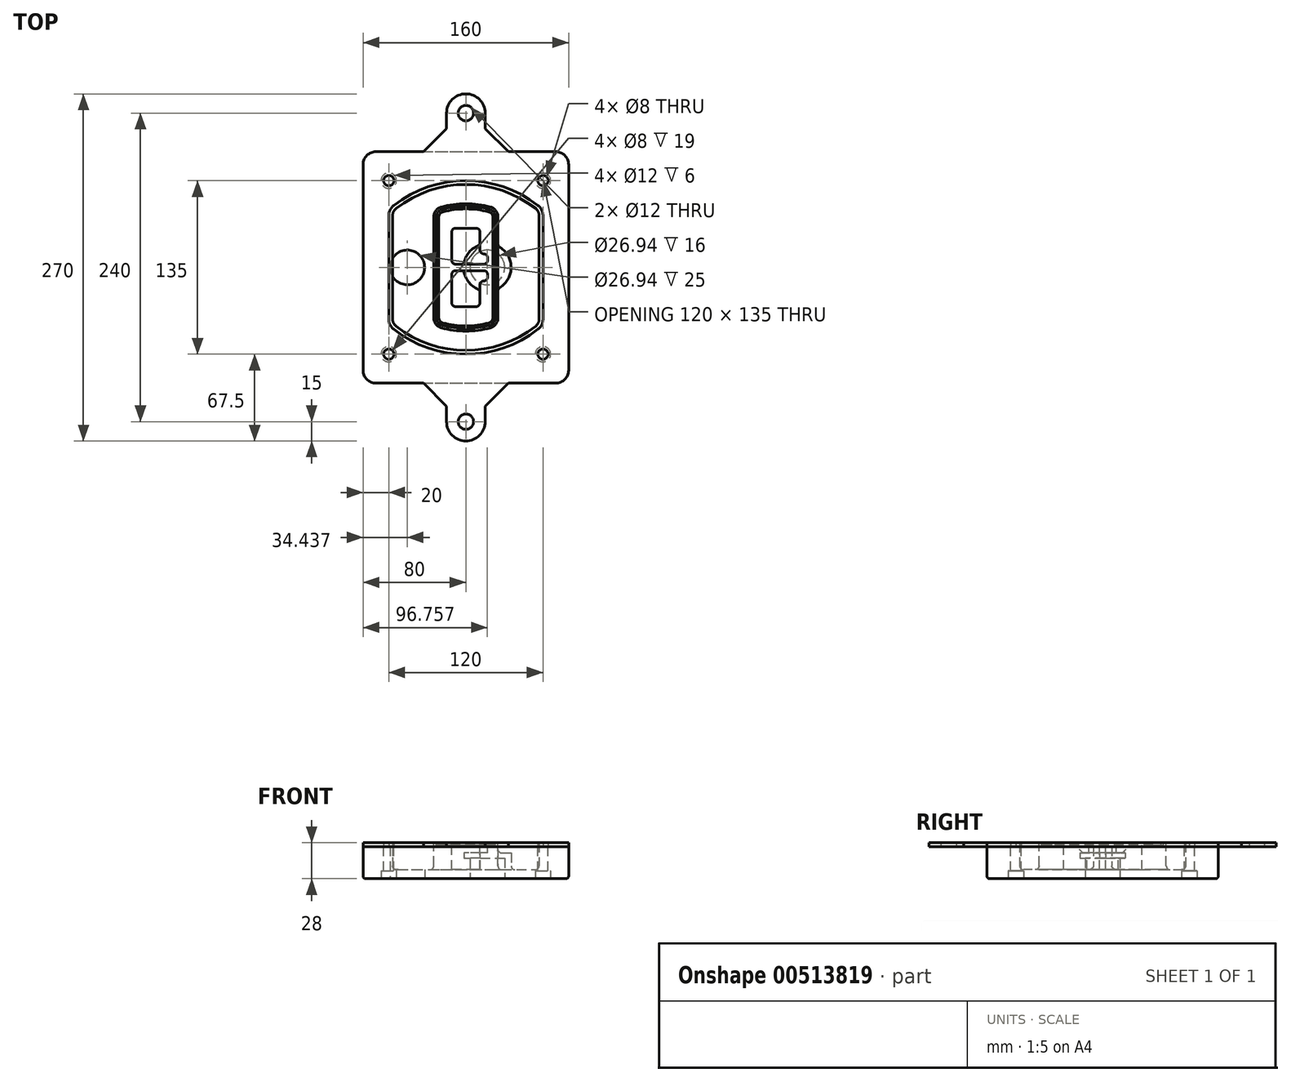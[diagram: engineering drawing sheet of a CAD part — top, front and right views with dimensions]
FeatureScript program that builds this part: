
annotation { "Feature Type Name" : "Feature", "Feature Type Description" : "" }
export const myFeature = defineFeature(function(context is Context, id is Id, definition is map)
    precondition{}
    {
        {
            var Q0;
            Q0=qCreatedBy(makeId("Top.planeOp"),FACE);
            var sketch = newSketch(context, id + "F0", { "sketchPlane" : qUnion([Q0])});
            skPoint(sketch, "E0.rect.middle", {"position": v(0, 0) * mm});
            skLineSegment(sketch, "E1.bottom", {"start": v(-70, -90) * mm, "end": v(70, -90) * mm});
            skLineSegment(sketch, "E1.top", {"start": v(-70, 90) * mm, "end": v(70, 90) * mm});
            skLineSegment(sketch, "E1.left", {"start": v(-80, -80) * mm, "end": v(-80, 80) * mm});
            skLineSegment(sketch, "E1.right", {"start": v(80, -80) * mm, "end": v(80, 80) * mm});
            skLineSegment(sketch, "E2", {"start": v(-80, 90) * mm, "end": v(80, -90) * mm, "construction": true});
            skLineSegment(sketch, "E3", {"start": v(80, 90) * mm, "end": v(-80, -90) * mm, "construction": true});
            skCircle(sketch, "E4", {"center": v(-60, 67.5) * mm, "radius": 4 * mm});
            skCircle(sketch, "E5", {"center": v(60, 67.5) * mm, "radius": 4 * mm});
            skCircle(sketch, "E6", {"center": v(60, -67.5) * mm, "radius": 4 * mm});
            skCircle(sketch, "E7", {"center": v(-60, -67.5) * mm, "radius": 4 * mm});
            skLineSegment(sketch, "E8", {"start": v(-60, 67.5) * mm, "end": v(60, 67.5) * mm, "construction": true});
            skLineSegment(sketch, "E9", {"start": v(60, 67.5) * mm, "end": v(60, -67.5) * mm, "construction": true});
            skLineSegment(sketch, "E10", {"start": v(60, -67.5) * mm, "end": v(-60, -67.5) * mm, "construction": true});
            skLineSegment(sketch, "E11", {"start": v(-60, -67.5) * mm, "end": v(-60, 67.5) * mm, "construction": true});
            skLineSegment(sketch, "E12", {"start": v(-60, 40.3) * mm, "end": v(-60, -40.3) * mm});
            skLineSegment(sketch, "E13", {"start": v(60, 40.3) * mm, "end": v(60, -40.3) * mm});
            skArc(sketch, "E14", {"start": v(56.15, 48.18) * mm, "mid": v(0, 67.5) * mm, "end": v(-56.15, 48.18) * mm});
            skArc(sketch, "E15", {"start": v(-56.15, -48.18) * mm, "mid": v(0, -67.5) * mm, "end": v(56.15, -48.18) * mm});
            skLineSegment(sketch, "E16", {"start": v(-60, 0) * mm, "end": v(60, 0) * mm, "construction": true});
            skPoint(sketch, "E17.visualSharp", {"position": v(-60, -45) * mm});
            skArc(sketch, "E17.filletArc", {"start": v(-60, -40.3) * mm, "mid": v(-58.99, -44.68) * mm, "end": v(-56.15, -48.18) * mm});
            skPoint(sketch, "E18.visualSharp", {"position": v(-60, 45) * mm});
            skArc(sketch, "E18.filletArc", {"start": v(-56.15, 48.18) * mm, "mid": v(-58.99, 44.68) * mm, "end": v(-60, 40.3) * mm});
            skPoint(sketch, "E19.visualSharp", {"position": v(60, 45) * mm});
            skArc(sketch, "E19.filletArc", {"start": v(60, 40.3) * mm, "mid": v(58.99, 44.68) * mm, "end": v(56.15, 48.18) * mm});
            skPoint(sketch, "E20.visualSharp", {"position": v(60, -45) * mm});
            skArc(sketch, "E20.filletArc", {"start": v(56.15, -48.18) * mm, "mid": v(58.99, -44.68) * mm, "end": v(60, -40.3) * mm});
            skPoint(sketch, "E21.visualSharp", {"position": v(-80, 90) * mm});
            skArc(sketch, "E21.filletArc", {"start": v(-70, 90) * mm, "mid": v(-77.07, 87.07) * mm, "end": v(-80, 80) * mm});
            skPoint(sketch, "E22.visualSharp", {"position": v(80, 90) * mm});
            skArc(sketch, "E22.filletArc", {"start": v(80, 80) * mm, "mid": v(77.07, 87.07) * mm, "end": v(70, 90) * mm});
            skPoint(sketch, "E23.visualSharp", {"position": v(80, -90) * mm});
            skArc(sketch, "E23.filletArc", {"start": v(70, -90) * mm, "mid": v(77.07, -87.07) * mm, "end": v(80, -80) * mm});
            skPoint(sketch, "E24.visualSharp", {"position": v(-80, -90) * mm});
            skArc(sketch, "E24.filletArc", {"start": v(-80, -80) * mm, "mid": v(-77.07, -87.07) * mm, "end": v(-70, -90) * mm});
            skArc(sketch, "E25.0", {"start": v(57, 40.3) * mm, "mid": v(56.3, 43.36) * mm, "end": v(54.3, 45.81) * mm});
            skLineSegment(sketch, "E25.1", {"start": v(57, 40.3) * mm, "end": v(57, -40.3) * mm});
            skArc(sketch, "E25.2", {"start": v(54.3, -45.81) * mm, "mid": v(56.3, -43.36) * mm, "end": v(57, -40.3) * mm});
            skArc(sketch, "E25.3", {"start": v(-54.3, -45.81) * mm, "mid": v(0, -64.5) * mm, "end": v(54.3, -45.81) * mm});
            skArc(sketch, "E25.4", {"start": v(-57, -40.3) * mm, "mid": v(-56.3, -43.36) * mm, "end": v(-54.3, -45.81) * mm});
            skArc(sketch, "E25.5", {"start": v(54.3, 45.81) * mm, "mid": v(0, 64.5) * mm, "end": v(-54.3, 45.81) * mm});
            skLineSegment(sketch, "E25.6", {"start": v(-57, 40.3) * mm, "end": v(-57, -40.3) * mm});
            skArc(sketch, "E25.7", {"start": v(-54.3, 45.81) * mm, "mid": v(-56.3, 43.36) * mm, "end": v(-57, 40.3) * mm});
            skArc(sketch, "E26.0", {"start": v(-58.62, 51.33) * mm, "mid": v(-62.58, 46.43) * mm, "end": v(-64, 40.3) * mm});
            skArc(sketch, "E26.1", {"start": v(58.62, 51.33) * mm, "mid": v(0, 71.5) * mm, "end": v(-58.62, 51.33) * mm});
            skArc(sketch, "E26.2", {"start": v(64, 40.3) * mm, "mid": v(62.58, 46.43) * mm, "end": v(58.62, 51.33) * mm});
            skLineSegment(sketch, "E26.3", {"start": v(64, 40.3) * mm, "end": v(64, -40.3) * mm});
            skArc(sketch, "E26.4", {"start": v(58.62, -51.33) * mm, "mid": v(62.58, -46.43) * mm, "end": v(64, -40.3) * mm});
            skLineSegment(sketch, "E26.5", {"start": v(-64, 40.3) * mm, "end": v(-64, -40.3) * mm});
            skArc(sketch, "E26.6", {"start": v(-58.62, -51.33) * mm, "mid": v(0, -71.5) * mm, "end": v(58.62, -51.33) * mm});
            skArc(sketch, "E26.7", {"start": v(-64, -40.3) * mm, "mid": v(-62.58, -46.43) * mm, "end": v(-58.62, -51.33) * mm});
            skSolve(sketch);
        }
        {
            var Q0;
            Q0=makeQuery(id+"F0.imprint","IMPRINT",FACE,{"disambiguationData":[TD([[makeQuery(id+"F0.imprint","IMPRINT",EDGE,{"derivedFrom":sQuery(id+"F0.wireOp",EDGE,"E1.bottom")}),1.0]])]});
            var Q1;
            Q1=makeQuery(id+"F0.imprint","IMPRINT",FACE,{"disambiguationData":[TD([[makeQuery(id+"F0.imprint","IMPRINT",EDGE,{"derivedFrom":sQuery(id+"F0.wireOp",EDGE,"E12")}),1.0]])]});
            var Q2;
            Q2=makeQuery(id+"F0.imprint","IMPRINT",FACE,{"disambiguationData":[TD([[makeQuery(id+"F0.imprint","IMPRINT",EDGE,{"derivedFrom":sQuery(id+"F0.wireOp",EDGE,"E25.0")}),1.0]])]});
            var Q3;
            Q3=makeQuery(id+"F0.imprint","IMPRINT",FACE,{"disambiguationData":[TD([[makeQuery(id+"F0.imprint","IMPRINT",EDGE,{"derivedFrom":sQuery(id+"F0.wireOp",EDGE,"E12")}),-1.0]])]});
            extrude(context, id + "F1", {"entities" : qUnion([Q0, Q1, Q2, Q3]), "oppositeDirection" : true, "depth" : 25 * mm});
        }
        {
            var Q0;
            Q0=makeQuery(id+"F0.imprint","IMPRINT",FACE,{"disambiguationData":[TD([[makeQuery(id+"F0.imprint","IMPRINT",EDGE,{"derivedFrom":sQuery(id+"F0.wireOp",EDGE,"E12")}),1.0]])]});
            extrude(context, id + "F2", {"entities" : qUnion([Q0]), "operationType" : NewBodyOperationType.ADD, "depth" : 3 * mm});
        }
        {
            var Q0;
            Q0=makeQuery(id+"F0.imprint","IMPRINT",FACE,{"disambiguationData":[TD([[makeQuery(id+"F0.imprint","IMPRINT",EDGE,{"derivedFrom":sQuery(id+"F0.wireOp",EDGE,"E25.0")}),1.0]])]});
            extrude(context, id + "F3", {"entities" : qUnion([Q0]), "operationType" : NewBodyOperationType.REMOVE, "oppositeDirection" : true, "depth" : 18 * mm});
        }
        {
            var Q0;
            Q0=makeQuery(id+"F2.opExtrude","CAP_FACE",FACE,{"disambiguationData":[OSD([sQuery(id+"F0.wireOp",EDGE,"E12"),sQuery(id+"F0.wireOp",EDGE,"E13"),sQuery(id+"F0.wireOp",EDGE,"E14"),sQuery(id+"F0.wireOp",EDGE,"E15"),sQuery(id+"F0.wireOp",EDGE,"E17.filletArc"),sQuery(id+"F0.wireOp",EDGE,"E18.filletArc"),sQuery(id+"F0.wireOp",EDGE,"E19.filletArc"),sQuery(id+"F0.wireOp",EDGE,"E20.filletArc"),sQuery(id+"F0.wireOp",EDGE,"E25.0"),sQuery(id+"F0.wireOp",EDGE,"E25.1"),sQuery(id+"F0.wireOp",EDGE,"E25.2"),sQuery(id+"F0.wireOp",EDGE,"E25.3"),sQuery(id+"F0.wireOp",EDGE,"E25.4"),sQuery(id+"F0.wireOp",EDGE,"E25.5"),sQuery(id+"F0.wireOp",EDGE,"E25.6"),sQuery(id+"F0.wireOp",EDGE,"E25.7")])],"isStart":false});
            var sketch = newSketch(context, id + "F4", { "sketchPlane" : qUnion([Q0])});
            skArc(sketch, "E27.0", {"start": v(-19.08, -46.97) * mm, "mid": v(0, -49.5) * mm, "end": v(19.08, -46.97) * mm});
            skArc(sketch, "E28.0", {"start": v(19.08, 46.97) * mm, "mid": v(0, 49.5) * mm, "end": v(-19.08, 46.97) * mm});
            skLineSegment(sketch, "E29", {"start": v(-25, 39.25) * mm, "end": v(-25, -39.25) * mm});
            skLineSegment(sketch, "E30", {"start": v(25, 39.25) * mm, "end": v(25, -39.25) * mm});
            skLineSegment(sketch, "E31", {"start": v(-25, 45.1) * mm, "end": v(25, 45.1) * mm, "construction": true});
            skLineSegment(sketch, "E32", {"start": v(-25, -45.1) * mm, "end": v(25, -45.1) * mm, "construction": true});
            skPoint(sketch, "E33.visualSharp", {"position": v(-25, 45.1) * mm});
            skArc(sketch, "E33.filletArc", {"start": v(-19.08, 46.97) * mm, "mid": v(-23.35, 44.11) * mm, "end": v(-25, 39.25) * mm});
            skPoint(sketch, "E34.visualSharp", {"position": v(25, 45.1) * mm});
            skArc(sketch, "E34.filletArc", {"start": v(25, 39.25) * mm, "mid": v(23.35, 44.11) * mm, "end": v(19.08, 46.97) * mm});
            skPoint(sketch, "E35.visualSharp", {"position": v(25, -45.1) * mm});
            skArc(sketch, "E35.filletArc", {"start": v(19.08, -46.97) * mm, "mid": v(23.35, -44.11) * mm, "end": v(25, -39.25) * mm});
            skPoint(sketch, "E36.visualSharp", {"position": v(-25, -45.1) * mm});
            skArc(sketch, "E36.filletArc", {"start": v(-25, -39.25) * mm, "mid": v(-23.35, -44.11) * mm, "end": v(-19.08, -46.97) * mm});
            skArc(sketch, "E37.0", {"start": v(54.3, 45.81) * mm, "mid": v(0, 64.5) * mm, "end": v(-54.3, 45.81) * mm});
            skArc(sketch, "E37.1", {"start": v(-54.3, 45.81) * mm, "mid": v(-56.3, 43.36) * mm, "end": v(-57, 40.3) * mm});
            skLineSegment(sketch, "E37.2", {"start": v(-57, 40.3) * mm, "end": v(-57, -40.3) * mm});
            skArc(sketch, "E37.3", {"start": v(-57, -40.3) * mm, "mid": v(-56.3, -43.36) * mm, "end": v(-54.3, -45.81) * mm});
            skArc(sketch, "E37.4", {"start": v(-54.3, -45.81) * mm, "mid": v(0, -64.5) * mm, "end": v(54.3, -45.81) * mm});
            skArc(sketch, "E37.5", {"start": v(54.3, -45.81) * mm, "mid": v(56.3, -43.36) * mm, "end": v(57, -40.3) * mm});
            skLineSegment(sketch, "E37.6", {"start": v(57, 40.3) * mm, "end": v(57, -40.3) * mm});
            skArc(sketch, "E37.7", {"start": v(57, 40.3) * mm, "mid": v(56.3, 43.36) * mm, "end": v(54.3, 45.81) * mm});
            skLineSegment(sketch, "E38.0", {"start": v(23, 39.25) * mm, "end": v(23, -39.25) * mm});
            skArc(sketch, "E38.1", {"start": v(18.56, -45.04) * mm, "mid": v(21.76, -42.9) * mm, "end": v(23, -39.25) * mm});
            skArc(sketch, "E38.2", {"start": v(-18.56, -45.04) * mm, "mid": v(0, -47.5) * mm, "end": v(18.56, -45.04) * mm});
            skArc(sketch, "E38.3", {"start": v(-23, -39.25) * mm, "mid": v(-21.76, -42.9) * mm, "end": v(-18.56, -45.04) * mm});
            skLineSegment(sketch, "E38.4", {"start": v(-23, 39.25) * mm, "end": v(-23, -39.25) * mm});
            skArc(sketch, "E38.5", {"start": v(23, 39.25) * mm, "mid": v(21.76, 42.9) * mm, "end": v(18.56, 45.04) * mm});
            skArc(sketch, "E38.6", {"start": v(-18.56, 45.04) * mm, "mid": v(-21.76, 42.9) * mm, "end": v(-23, 39.25) * mm});
            skArc(sketch, "E38.7", {"start": v(18.56, 45.04) * mm, "mid": v(0, 47.5) * mm, "end": v(-18.56, 45.04) * mm});
            skArc(sketch, "E39.0", {"start": v(21, 39.25) * mm, "mid": v(20.18, 41.68) * mm, "end": v(18.04, 43.1) * mm});
            skLineSegment(sketch, "E39.1", {"start": v(21, 39.25) * mm, "end": v(21, -39.25) * mm});
            skArc(sketch, "E39.2", {"start": v(18.04, -43.1) * mm, "mid": v(20.18, -41.68) * mm, "end": v(21, -39.25) * mm});
            skArc(sketch, "E39.3", {"start": v(-18.04, -43.1) * mm, "mid": v(0, -45.5) * mm, "end": v(18.04, -43.1) * mm});
            skArc(sketch, "E39.4", {"start": v(-21, -39.25) * mm, "mid": v(-20.18, -41.68) * mm, "end": v(-18.04, -43.1) * mm});
            skArc(sketch, "E39.5", {"start": v(18.04, 43.1) * mm, "mid": v(0, 45.5) * mm, "end": v(-18.04, 43.1) * mm});
            skLineSegment(sketch, "E39.6", {"start": v(-21, 39.25) * mm, "end": v(-21, -39.25) * mm});
            skArc(sketch, "E39.7", {"start": v(-18.04, 43.1) * mm, "mid": v(-20.18, 41.68) * mm, "end": v(-21, 39.25) * mm});
            skLineSegment(sketch, "E40", {"start": v(-25, 0) * mm, "end": v(25, 0) * mm, "construction": true});
            skLineSegment(sketch, "E41", {"start": v(-11, 5.5) * mm, "end": v(-11, 27.5) * mm});
            skLineSegment(sketch, "E42", {"start": v(-8, 30.5) * mm, "end": v(8, 30.5) * mm});
            skLineSegment(sketch, "E43", {"start": v(11, 27.5) * mm, "end": v(11, 13.5) * mm});
            skLineSegment(sketch, "E44", {"start": v(14, 10.5) * mm, "end": v(14, 10.5) * mm});
            skLineSegment(sketch, "E45", {"start": v(17, 7.5) * mm, "end": v(17, 5.5) * mm});
            skLineSegment(sketch, "E46", {"start": v(14, 2.5) * mm, "end": v(-8, 2.5) * mm});
            skPoint(sketch, "E47.visualSharp", {"position": v(-11, 30.5) * mm});
            skArc(sketch, "E47.filletArc", {"start": v(-8, 30.5) * mm, "mid": v(-10.12, 29.62) * mm, "end": v(-11, 27.5) * mm});
            skPoint(sketch, "E48.visualSharp", {"position": v(11, 30.5) * mm});
            skArc(sketch, "E48.filletArc", {"start": v(11, 27.5) * mm, "mid": v(10.12, 29.62) * mm, "end": v(8, 30.5) * mm});
            skPoint(sketch, "E49.visualSharp", {"position": v(11, 10.5) * mm});
            skArc(sketch, "E49.filletArc", {"start": v(11, 13.5) * mm, "mid": v(11.88, 11.38) * mm, "end": v(14, 10.5) * mm});
            skPoint(sketch, "E50.visualSharp", {"position": v(17, 10.5) * mm});
            skArc(sketch, "E50.filletArc", {"start": v(17, 7.5) * mm, "mid": v(16.12, 9.62) * mm, "end": v(14, 10.5) * mm});
            skPoint(sketch, "E51.visualSharp", {"position": v(17, 2.5) * mm});
            skArc(sketch, "E51.filletArc", {"start": v(14, 2.5) * mm, "mid": v(16.12, 3.38) * mm, "end": v(17, 5.5) * mm});
            skPoint(sketch, "E52.visualSharp", {"position": v(-11, 2.5) * mm});
            skArc(sketch, "E52.filletArc", {"start": v(-11, 5.5) * mm, "mid": v(-10.12, 3.38) * mm, "end": v(-8, 2.5) * mm});
            skLineSegment(sketch, "E53.0.MirrorCS", {"start": v(14, -2.5) * mm, "end": v(-8, -2.5) * mm});
            skArc(sketch, "E54.0.MirrorCS", {"start": v(-11, -5.5) * mm, "mid": v(-10.12, -3.38) * mm, "end": v(-8, -2.5) * mm});
            skLineSegment(sketch, "E55.0.MirrorCS", {"start": v(-11, -5.5) * mm, "end": v(-11, -27.5) * mm});
            skArc(sketch, "E56.0.MirrorCS", {"start": v(-8, -30.5) * mm, "mid": v(-10.12, -29.62) * mm, "end": v(-11, -27.5) * mm});
            skLineSegment(sketch, "E57.0.MirrorCS", {"start": v(-8, -30.5) * mm, "end": v(8, -30.5) * mm});
            skArc(sketch, "E58.0.MirrorCS", {"start": v(11, -27.5) * mm, "mid": v(10.12, -29.62) * mm, "end": v(8, -30.5) * mm});
            skLineSegment(sketch, "E59.0.MirrorCS", {"start": v(11, -27.5) * mm, "end": v(11, -13.5) * mm});
            skArc(sketch, "E60.0.MirrorCS", {"start": v(11, -13.5) * mm, "mid": v(11.88, -11.38) * mm, "end": v(14, -10.5) * mm});
            skArc(sketch, "E61.0.MirrorCS", {"start": v(17, -7.5) * mm, "mid": v(16.12, -9.62) * mm, "end": v(14, -10.5) * mm});
            skLineSegment(sketch, "E62.0.MirrorCS", {"start": v(17, -7.5) * mm, "end": v(17, -5.5) * mm});
            skArc(sketch, "E63.0.MirrorCS", {"start": v(14, -2.5) * mm, "mid": v(16.12, -3.38) * mm, "end": v(17, -5.5) * mm});
            skSolve(sketch);
        }
        {
            var Q0;
            Q0=makeQuery(id+"F4.imprint","IMPRINT",FACE,{"disambiguationData":[TD([[makeQuery(id+"F4.imprint","IMPRINT",EDGE,{"derivedFrom":sQuery(id+"F4.wireOp",EDGE,"E27.0")}),1.0]])]});
            var Q1;
            Q1=makeQuery(id+"F4.imprint","IMPRINT",FACE,{"disambiguationData":[TD([[makeQuery(id+"F4.imprint","IMPRINT",EDGE,{"derivedFrom":sQuery(id+"F4.wireOp",EDGE,"E38.0")}),-1.0]])]});
            var Q2;
            Q2=makeQuery(id+"F4.imprint","IMPRINT",FACE,{"disambiguationData":[TD([[makeQuery(id+"F4.imprint","IMPRINT",EDGE,{"derivedFrom":sQuery(id+"F4.wireOp",EDGE,"E39.0")}),1.0]])]});
            extrude(context, id + "F5", {"entities" : qUnion([Q0, Q1, Q2]), "operationType" : NewBodyOperationType.ADD, "endBound" : BoundingType.UP_TO_NEXT, "oppositeDirection" : true, "depth" : 25 * mm});
        }
        {
            var Q0;
            Q0=makeQuery(id+"F4.imprint","IMPRINT",FACE,{"disambiguationData":[TD([[makeQuery(id+"F4.imprint","IMPRINT",EDGE,{"derivedFrom":sQuery(id+"F4.wireOp",EDGE,"E38.0")}),-1.0]])]});
            extrude(context, id + "F6", {"entities" : qUnion([Q0]), "operationType" : NewBodyOperationType.REMOVE, "oppositeDirection" : true, "depth" : 2 * mm});
        }
        {
            var Q0;
            Q0=makeQuery(id+"F1.opExtrude","CAP_FACE",FACE,{"disambiguationData":[OSD([sQuery(id+"F0.wireOp",EDGE,"E1.bottom"),sQuery(id+"F0.wireOp",EDGE,"E1.top"),sQuery(id+"F0.wireOp",EDGE,"E1.left"),sQuery(id+"F0.wireOp",EDGE,"E1.right"),sQuery(id+"F0.wireOp",EDGE,"E4"),sQuery(id+"F0.wireOp",EDGE,"E5"),sQuery(id+"F0.wireOp",EDGE,"E6"),sQuery(id+"F0.wireOp",EDGE,"E7"),sQuery(id+"F0.wireOp",EDGE,"E21.filletArc"),sQuery(id+"F0.wireOp",EDGE,"E22.filletArc"),sQuery(id+"F0.wireOp",EDGE,"E23.filletArc"),sQuery(id+"F0.wireOp",EDGE,"E24.filletArc")])],"isStart":false});
            var sketch = newSketch(context, id + "F7", { "sketchPlane" : qUnion([Q0])});
            skCircle(sketch, "E64", {"center": v(16.76, 0) * mm, "radius": 13.47 * mm});
            skCircle(sketch, "E65", {"center": v(-45.56, 0) * mm, "radius": 13.47 * mm});
            skLineSegment(sketch, "E66", {"start": v(80, 0) * mm, "end": v(-80, 0) * mm});
            skCircle(sketch, "E67", {"center": v(16.76, 0) * mm, "radius": 18.47 * mm});
            skCircle(sketch, "E68", {"center": v(60, -67.5) * mm, "radius": 6 * mm});
            skCircle(sketch, "E69", {"center": v(-60, -67.5) * mm, "radius": 6 * mm});
            skCircle(sketch, "E70", {"center": v(-60, 67.5) * mm, "radius": 6 * mm});
            skCircle(sketch, "E71", {"center": v(60, 67.5) * mm, "radius": 6 * mm});
            skSolve(sketch);
        }
        {
            var Q0;
            {var subQ1=sQuery(id+"F7.wireOp",EDGE,"E66");var subQ4=sQuery(id+"F7.wireOp",EDGE,"E64");var subQ6=makeQuery(id+"F7.imprint","INTERSECT",VERTEX,{"disambiguationData":[OD(0.0)],"derivedFrom":[subQ4,subQ1]});Q0=makeQuery(id+"F7.imprint","IMPRINT",FACE,{"disambiguationData":[TD([[makeQuery(id+"F7.imprint","IMPRINT",EDGE,{"disambiguationData":[TD([[subQ6,-1.0]])],"derivedFrom":subQ4}),-1.0]])]});}
            var Q1;
            {var subQ0=sQuery(id+"F7.wireOp",EDGE,"E66");var subQ1=sQuery(id+"F7.wireOp",EDGE,"E64");var subQ3=makeQuery(id+"F7.imprint","INTERSECT",VERTEX,{"disambiguationData":[OD(0.0)],"derivedFrom":[subQ1,subQ0]});Q1=makeQuery(id+"F7.imprint","IMPRINT",FACE,{"disambiguationData":[TD([[makeQuery(id+"F7.imprint","IMPRINT",EDGE,{"disambiguationData":[TD([[subQ3,-1.0]])],"derivedFrom":subQ1}),1.0]])]});}
            var Q2;
            {var subQ0=sQuery(id+"F7.wireOp",EDGE,"E66");var subQ1=sQuery(id+"F7.wireOp",EDGE,"E64");var subQ3=makeQuery(id+"F7.imprint","INTERSECT",VERTEX,{"disambiguationData":[OD(0.0)],"derivedFrom":[subQ1,subQ0]});Q2=makeQuery(id+"F7.imprint","IMPRINT",FACE,{"disambiguationData":[TD([[makeQuery(id+"F7.imprint","IMPRINT",EDGE,{"disambiguationData":[TD([[subQ3,1.0]])],"derivedFrom":subQ1}),1.0]])]});}
            var Q3;
            {var subQ1=sQuery(id+"F7.wireOp",EDGE,"E66");var subQ4=sQuery(id+"F7.wireOp",EDGE,"E64");var subQ6=makeQuery(id+"F7.imprint","INTERSECT",VERTEX,{"disambiguationData":[OD(0.0)],"derivedFrom":[subQ4,subQ1]});Q3=makeQuery(id+"F7.imprint","IMPRINT",FACE,{"disambiguationData":[TD([[makeQuery(id+"F7.imprint","IMPRINT",EDGE,{"disambiguationData":[TD([[subQ6,1.0]])],"derivedFrom":subQ4}),-1.0]])]});}
            extrude(context, id + "F8", {"entities" : qUnion([Q0, Q1, Q2, Q3]), "operationType" : NewBodyOperationType.ADD, "oppositeDirection" : true, "depth" : 20 * mm});
        }
        {
            var Q0;
            {var subQ0=sQuery(id+"F7.wireOp",EDGE,"E66");var subQ1=sQuery(id+"F7.wireOp",EDGE,"E64");var subQ3=makeQuery(id+"F7.imprint","INTERSECT",VERTEX,{"disambiguationData":[OD(0.0)],"derivedFrom":[subQ1,subQ0]});Q0=makeQuery(id+"F7.imprint","IMPRINT",FACE,{"disambiguationData":[TD([[makeQuery(id+"F7.imprint","IMPRINT",EDGE,{"disambiguationData":[TD([[subQ3,-1.0]])],"derivedFrom":subQ1}),1.0]])]});}
            var Q1;
            {var subQ0=sQuery(id+"F7.wireOp",EDGE,"E66");var subQ1=sQuery(id+"F7.wireOp",EDGE,"E64");var subQ3=makeQuery(id+"F7.imprint","INTERSECT",VERTEX,{"disambiguationData":[OD(0.0)],"derivedFrom":[subQ1,subQ0]});Q1=makeQuery(id+"F7.imprint","IMPRINT",FACE,{"disambiguationData":[TD([[makeQuery(id+"F7.imprint","IMPRINT",EDGE,{"disambiguationData":[TD([[subQ3,1.0]])],"derivedFrom":subQ1}),1.0]])]});}
            extrude(context, id + "F9", {"entities" : qUnion([Q0, Q1]), "operationType" : NewBodyOperationType.REMOVE, "oppositeDirection" : true, "depth" : 16 * mm});
        }
        {
            var Q0;
            {var subQ0=sQuery(id+"F7.wireOp",EDGE,"E66");var subQ1=sQuery(id+"F7.wireOp",EDGE,"E65");var subQ3=makeQuery(id+"F7.imprint","INTERSECT",VERTEX,{"disambiguationData":[OD(0.0)],"derivedFrom":[subQ1,subQ0]});Q0=makeQuery(id+"F7.imprint","IMPRINT",FACE,{"disambiguationData":[TD([[makeQuery(id+"F7.imprint","IMPRINT",EDGE,{"disambiguationData":[TD([[subQ3,-1.0]])],"derivedFrom":subQ1}),1.0]])]});}
            var Q1;
            {var subQ0=sQuery(id+"F7.wireOp",EDGE,"E66");var subQ1=sQuery(id+"F7.wireOp",EDGE,"E65");var subQ3=makeQuery(id+"F7.imprint","INTERSECT",VERTEX,{"disambiguationData":[OD(0.0)],"derivedFrom":[subQ1,subQ0]});Q1=makeQuery(id+"F7.imprint","IMPRINT",FACE,{"disambiguationData":[TD([[makeQuery(id+"F7.imprint","IMPRINT",EDGE,{"disambiguationData":[TD([[subQ3,1.0]])],"derivedFrom":subQ1}),1.0]])]});}
            extrude(context, id + "F10", {"entities" : qUnion([Q0, Q1]), "operationType" : NewBodyOperationType.REMOVE, "oppositeDirection" : true, "depth" : 25 * mm});
        }
        {
            var Q0;
            Q0=makeQuery(id+"F7.imprint","IMPRINT",FACE,{"disambiguationData":[TD([[makeQuery(id+"F7.imprint","IMPRINT",EDGE,{"derivedFrom":sQuery(id+"F7.wireOp",EDGE,"E68")}),1.0]])]});
            var Q1;
            Q1=makeQuery(id+"F7.imprint","IMPRINT",FACE,{"disambiguationData":[TD([[makeQuery(id+"F7.imprint","IMPRINT",EDGE,{"derivedFrom":makeQuery(id+"F1.opExtrude","CAP_EDGE",EDGE,{"disambiguationData":[OSD([sQuery(id+"F0.wireOp",EDGE,"E5")])],"isStart":false})}),-1.0]])]});
            var Q2;
            Q2=makeQuery(id+"F7.imprint","IMPRINT",FACE,{"disambiguationData":[TD([[makeQuery(id+"F7.imprint","IMPRINT",EDGE,{"derivedFrom":sQuery(id+"F7.wireOp",EDGE,"E69")}),1.0]])]});
            var Q3;
            Q3=makeQuery(id+"F7.imprint","IMPRINT",FACE,{"disambiguationData":[TD([[makeQuery(id+"F7.imprint","IMPRINT",EDGE,{"derivedFrom":makeQuery(id+"F1.opExtrude","CAP_EDGE",EDGE,{"disambiguationData":[OSD([sQuery(id+"F0.wireOp",EDGE,"E4")])],"isStart":false})}),-1.0]])]});
            var Q4;
            Q4=makeQuery(id+"F7.imprint","IMPRINT",FACE,{"disambiguationData":[TD([[makeQuery(id+"F7.imprint","IMPRINT",EDGE,{"derivedFrom":sQuery(id+"F7.wireOp",EDGE,"E70")}),1.0]])]});
            var Q5;
            Q5=makeQuery(id+"F7.imprint","IMPRINT",FACE,{"disambiguationData":[TD([[makeQuery(id+"F7.imprint","IMPRINT",EDGE,{"derivedFrom":makeQuery(id+"F1.opExtrude","CAP_EDGE",EDGE,{"disambiguationData":[OSD([sQuery(id+"F0.wireOp",EDGE,"E7")])],"isStart":false})}),-1.0]])]});
            var Q6;
            Q6=makeQuery(id+"F7.imprint","IMPRINT",FACE,{"disambiguationData":[TD([[makeQuery(id+"F7.imprint","IMPRINT",EDGE,{"derivedFrom":sQuery(id+"F7.wireOp",EDGE,"E71")}),1.0]])]});
            var Q7;
            Q7=makeQuery(id+"F7.imprint","IMPRINT",FACE,{"disambiguationData":[TD([[makeQuery(id+"F7.imprint","IMPRINT",EDGE,{"derivedFrom":makeQuery(id+"F1.opExtrude","CAP_EDGE",EDGE,{"disambiguationData":[OSD([sQuery(id+"F0.wireOp",EDGE,"E6")])],"isStart":false})}),-1.0]])]});
            extrude(context, id + "F11", {"entities" : qUnion([Q0, Q1, Q2, Q3, Q4, Q5, Q6, Q7]), "operationType" : NewBodyOperationType.REMOVE, "oppositeDirection" : true, "depth" : 6 * mm});
        }
        {
            var Q0;
            Q0=makeQuery(id+"F9.boolean.opBoolean","COPY",FACE,{"derivedFrom":makeQuery(id+"F9.opExtrude","CAP_FACE",FACE,{"disambiguationData":[OSD([sQuery(id+"F7.wireOp",EDGE,"E64")])],"isStart":false})});
            var sketch = newSketch(context, id + "F12", { "sketchPlane" : qUnion([Q0])});
            skArc(sketch, "E72.0", {"start": v(11, 17.55) * mm, "mid": v(2.57, 11.82) * mm, "end": v(-1.54, 2.5) * mm});
            skArc(sketch, "E72.1", {"start": v(-1.54, -2.5) * mm, "mid": v(2.57, -11.82) * mm, "end": v(11, -17.55) * mm});
            skLineSegment(sketch, "E73", {"start": v(-1.54, -2.5) * mm, "end": v(14, -2.5) * mm});
            skLineSegment(sketch, "E74.0", {"start": v(14, 2.5) * mm, "end": v(-1.54, 2.5) * mm});
            skArc(sketch, "E74.1", {"start": v(14, 2.5) * mm, "mid": v(16.12, 3.38) * mm, "end": v(17, 5.5) * mm});
            skLineSegment(sketch, "E74.2", {"start": v(17, 7.5) * mm, "end": v(17, 5.5) * mm});
            skArc(sketch, "E74.3", {"start": v(17, 7.5) * mm, "mid": v(16.12, 9.62) * mm, "end": v(14, 10.5) * mm});
            skArc(sketch, "E74.4", {"start": v(11, 13.5) * mm, "mid": v(11.88, 11.38) * mm, "end": v(14, 10.5) * mm});
            skLineSegment(sketch, "E74.5", {"start": v(11, 17.55) * mm, "end": v(11, 13.5) * mm});
            skLineSegment(sketch, "E74.7", {"start": v(14, -2.5) * mm, "end": v(-1.54, -2.5) * mm});
            skArc(sketch, "E74.8", {"start": v(14, -2.5) * mm, "mid": v(16.12, -3.38) * mm, "end": v(17, -5.5) * mm});
            skLineSegment(sketch, "E74.9", {"start": v(17, -7.5) * mm, "end": v(17, -5.5) * mm});
            skArc(sketch, "E74.10", {"start": v(17, -7.5) * mm, "mid": v(16.12, -9.62) * mm, "end": v(14, -10.5) * mm});
            skArc(sketch, "E74.11", {"start": v(11, -13.5) * mm, "mid": v(11.88, -11.38) * mm, "end": v(14, -10.5) * mm});
            skLineSegment(sketch, "E74.12", {"start": v(11, -17.55) * mm, "end": v(11, -13.5) * mm});
            skPoint(sketch, "E75.orphan", {"position": v(11, -27.5) * mm});
            skPoint(sketch, "E76.orphan", {"position": v(-8, -2.5) * mm});
            skPoint(sketch, "E77.orphan", {"position": v(-8, 2.5) * mm});
            skPoint(sketch, "E78.orphan", {"position": v(11, 27.5) * mm});
            skSolve(sketch);
        }
        {
            var Q0;
            {var subQ7=sQuery(id+"F12.wireOp",EDGE,"E72.0");var subQ14=sQuery(id+"F12.wireOp",EDGE,"E72.1");var subQ16=sQuery(id+"F12.wireOp",EDGE,"E74.1");var subQ18=sQuery(id+"F12.wireOp",EDGE,"E74.8");Q0=qUnion([makeQuery(id+"F12.imprint","IMPRINT",FACE,{"disambiguationData":[TD([[makeQuery(id+"F12.imprint","IMPRINT",EDGE,{"derivedFrom":subQ7}),1.0]])]}),makeQuery(id+"F12.imprint","IMPRINT",FACE,{"disambiguationData":[TD([[makeQuery(id+"F12.imprint","IMPRINT",EDGE,{"derivedFrom":subQ14}),1.0]])]}),makeQuery(id+"F12.imprint","IMPRINT",FACE,{"disambiguationData":[TD([[makeQuery(id+"F12.imprint","IMPRINT",EDGE,{"derivedFrom":subQ16}),1.0]])]}),makeQuery(id+"F12.imprint","IMPRINT",FACE,{"disambiguationData":[TD([[makeQuery(id+"F12.imprint","IMPRINT",EDGE,{"derivedFrom":subQ18}),-1.0]])]})]);}
            var Q1;
            Q1=makeQuery(id+"F5.boolean.opBoolean","SPLIT",FACE,{"disambiguationData":[TD([makeQuery(id+"F5.opExtrude","SWEPT_FACE",FACE,{"disambiguationData":[OSD([sQuery(id+"F4.wireOp",EDGE,"E41")])]})])],"derivedFrom":makeQuery(id+"F3.boolean.opBoolean","COPY",FACE,{"derivedFrom":makeQuery(id+"F3.opExtrude","CAP_FACE",FACE,{"disambiguationData":[OSD([sQuery(id+"F0.wireOp",EDGE,"E25.0"),sQuery(id+"F0.wireOp",EDGE,"E25.1"),sQuery(id+"F0.wireOp",EDGE,"E25.2"),sQuery(id+"F0.wireOp",EDGE,"E25.3"),sQuery(id+"F0.wireOp",EDGE,"E25.4"),sQuery(id+"F0.wireOp",EDGE,"E25.5"),sQuery(id+"F0.wireOp",EDGE,"E25.6"),sQuery(id+"F0.wireOp",EDGE,"E25.7")])],"isStart":false})})});
            extrude(context, id + "F13", {"entities" : qUnion([Q0]), "operationType" : NewBodyOperationType.REMOVE, "endBound" : BoundingType.UP_TO_SURFACE, "endBoundEntityFace" : qUnion([Q1]), "depth" : 25 * mm});
        }
        {
            var Q0;
            Q0=makeQuery(id+"F3.boolean.opBoolean","COPY",EDGE,{"derivedFrom":makeQuery(id+"F3.opExtrude","CAP_EDGE",EDGE,{"disambiguationData":[OSD([sQuery(id+"F0.wireOp",EDGE,"E25.6")])],"isStart":false})});
            var Q1;
            Q1=makeQuery(id+"F8.boolean.opBoolean","INTERSECT",EDGE,{"derivedFrom":[makeQuery(id+"F5.opExtrude","SWEPT_FACE",FACE,{"disambiguationData":[OSD([sQuery(id+"F4.wireOp",EDGE,"E30")])]}),makeQuery(id+"F8.opExtrude","CAP_FACE",FACE,{"disambiguationData":[OSD([sQuery(id+"F7.wireOp",EDGE,"E67")])],"isStart":false})]});
            var Q2;
            Q2=makeQuery(id+"F8.boolean.opBoolean","INTERSECT",EDGE,{"disambiguationData":[OD(1.0)],"derivedFrom":[makeQuery(id+"F5.opExtrude","SWEPT_FACE",FACE,{"disambiguationData":[OSD([sQuery(id+"F4.wireOp",EDGE,"E30")])]}),makeQuery(id+"F8.opExtrude","SWEPT_FACE",FACE,{"disambiguationData":[OSD([sQuery(id+"F7.wireOp",EDGE,"E67")])]})]});
            var Q3;
            {var subQ0=sQuery(id+"F4.wireOp",EDGE,"E30");Q3=makeQuery(id+"F8.boolean.opBoolean","SPLIT",EDGE,{"disambiguationData":[TD([makeQuery(id+"F5.opExtrude","SWEPT_FACE",FACE,{"disambiguationData":[OSD([sQuery(id+"F4.wireOp",EDGE,"E35.filletArc")])]})])],"derivedFrom":makeQuery(id+"F5.opExtrude","CAP_EDGE",EDGE,{"disambiguationData":[OSD([subQ0])],"isStart":false})});}
            var Q4;
            {var subQ0=sQuery(id+"F0.wireOp",EDGE,"E25.7");var subQ1=sQuery(id+"F0.wireOp",EDGE,"E25.1");var subQ2=sQuery(id+"F0.wireOp",EDGE,"E25.6");var subQ3=sQuery(id+"F0.wireOp",EDGE,"E25.5");var subQ4=sQuery(id+"F0.wireOp",EDGE,"E25.4");var subQ5=sQuery(id+"F0.wireOp",EDGE,"E25.0");var subQ6=sQuery(id+"F0.wireOp",EDGE,"E25.2");var subQ7=sQuery(id+"F0.wireOp",EDGE,"E25.3");Q4=makeQuery(id+"F8.boolean.opBoolean","INTERSECT",EDGE,{"derivedFrom":[makeQuery(id+"F5.boolean.opBoolean","SPLIT",FACE,{"disambiguationData":[TD([makeQuery(id+"F2.opExtrude","SWEPT_FACE",FACE,{"disambiguationData":[OSD([subQ5])]})])],"derivedFrom":makeQuery(id+"F3.boolean.opBoolean","COPY",FACE,{"derivedFrom":makeQuery(id+"F3.opExtrude","CAP_FACE",FACE,{"disambiguationData":[OSD([subQ5,subQ1,subQ6,subQ7,subQ4,subQ3,subQ2,subQ0])],"isStart":false})})}),makeQuery(id+"F8.opExtrude","SWEPT_FACE",FACE,{"disambiguationData":[OSD([sQuery(id+"F7.wireOp",EDGE,"E67")])]})]});}
            var Q5;
            Q5=makeQuery(id+"F8.boolean.opBoolean","INTERSECT",EDGE,{"disambiguationData":[OD(0.0)],"derivedFrom":[makeQuery(id+"F5.opExtrude","SWEPT_FACE",FACE,{"disambiguationData":[OSD([sQuery(id+"F4.wireOp",EDGE,"E30")])]}),makeQuery(id+"F8.opExtrude","SWEPT_FACE",FACE,{"disambiguationData":[OSD([sQuery(id+"F7.wireOp",EDGE,"E67")])]})]});
            fillet(context, id + "F14", {"entities" : qUnion([Q0, Q1, Q2, Q3, Q4, Q5]), "radius" : 3 * mm, "tangentPropagation" : true, "allowEdgeOverflow" : false});
        }
        {
            var Q0;
            Q0=makeQuery(id+"F1.opExtrude","CAP_EDGE",EDGE,{"disambiguationData":[OSD([sQuery(id+"F0.wireOp",EDGE,"E1.bottom")])],"isStart":false});
            fillet(context, id + "F15", {"entities" : qUnion([Q0]), "radius" : 2 * mm, "tangentPropagation" : true, "allowEdgeOverflow" : false});
        }
        {
            var Q0;
            {var subQ0=sQuery(id+"F0.wireOp",EDGE,"E21.filletArc");var subQ1=sQuery(id+"F0.wireOp",EDGE,"E7");var subQ2=sQuery(id+"F0.wireOp",EDGE,"E6");var subQ3=sQuery(id+"F0.wireOp",EDGE,"E5");var subQ4=sQuery(id+"F0.wireOp",EDGE,"E4");var subQ5=sQuery(id+"F0.wireOp",EDGE,"E22.filletArc");var subQ6=sQuery(id+"F0.wireOp",EDGE,"E1.bottom");var subQ7=sQuery(id+"F0.wireOp",EDGE,"E1.right");var subQ8=sQuery(id+"F0.wireOp",EDGE,"E1.top");var subQ9=sQuery(id+"F0.wireOp",EDGE,"E1.left");var subQ10=sQuery(id+"F0.wireOp",EDGE,"E23.filletArc");var subQ11=sQuery(id+"F0.wireOp",EDGE,"E24.filletArc");Q0=makeQuery(id+"F2.boolean.opBoolean","SPLIT",FACE,{"disambiguationData":[TD([makeQuery(id+"F1.opExtrude","SWEPT_FACE",FACE,{"disambiguationData":[OSD([subQ6])]})])],"derivedFrom":makeQuery(id+"F1.opExtrude","CAP_FACE",FACE,{"disambiguationData":[OSD([subQ6,subQ8,subQ9,subQ7,subQ4,subQ3,subQ2,subQ1,subQ0,subQ5,subQ10,subQ11])],"isStart":true})});}
            var sketch = newSketch(context, id + "F16", { "sketchPlane" : qUnion([Q0])});
            skLineSegment(sketch, "E79", {"start": v(0, 90) * mm, "end": v(0, 120) * mm, "construction": true});
            skCircle(sketch, "E80", {"center": v(0, 120) * mm, "radius": 6 * mm});
            skLineSegment(sketch, "E81", {"start": v(-33, 90) * mm, "end": v(-15, 108) * mm});
            skLineSegment(sketch, "E82", {"start": v(-15, 108) * mm, "end": v(-15, 120) * mm});
            skArc(sketch, "E83", {"start": v(-15, 120) * mm, "mid": v(0, 135) * mm, "end": v(15, 120) * mm});
            skLineSegment(sketch, "E84", {"start": v(15, 120) * mm, "end": v(15, 108) * mm});
            skLineSegment(sketch, "E85", {"start": v(15, 108) * mm, "end": v(33, 90) * mm});
            skLineSegment(sketch, "E86", {"start": v(80, 0) * mm, "end": v(-80, 0) * mm, "construction": true});
            skLineSegment(sketch, "E87.MirrorCS", {"start": v(15, -108) * mm, "end": v(33, -90) * mm});
            skLineSegment(sketch, "E88.MirrorCS", {"start": v(-33, -90) * mm, "end": v(-15, -108) * mm});
            skLineSegment(sketch, "E89.MirrorCS", {"start": v(-15, -108) * mm, "end": v(-15, -120) * mm});
            skArc(sketch, "E90.MirrorCS", {"start": v(-15, -120) * mm, "mid": v(0, -135) * mm, "end": v(15, -120) * mm});
            skCircle(sketch, "E91.MirrorC", {"center": v(0, -120) * mm, "radius": 6 * mm});
            skLineSegment(sketch, "E92.MirrorCS", {"start": v(15, -120) * mm, "end": v(15, -108) * mm});
            skLineSegment(sketch, "E93.MirrorCS", {"start": v(0, -90) * mm, "end": v(0, -120) * mm, "construction": true});
            skSolve(sketch);
        }
        {
            var Q0;
            Q0=makeQuery(id+"F16.imprint","IMPRINT",FACE,{"disambiguationData":[TD([[makeQuery(id+"F16.imprint","IMPRINT",EDGE,{"derivedFrom":sQuery(id+"F16.wireOp",EDGE,"E80")}),-1.0]])]});
            var Q1;
            {var subQ1=sQuery(id+"F16.wireOp",EDGE,"E87.MirrorCS");Q1=makeQuery(id+"F16.imprint","IMPRINT",FACE,{"disambiguationData":[TD([[makeQuery(id+"F16.imprint","IMPRINT",EDGE,{"derivedFrom":subQ1}),1.0]])]});}
            var Q2;
            Q2=makeQuery(id+"F16.imprint","IMPRINT",FACE,{"disambiguationData":[TD([[makeQuery(id+"F16.imprint","IMPRINT",EDGE,{"derivedFrom":makeQuery(id+"F1.opExtrude","CAP_EDGE",EDGE,{"disambiguationData":[OSD([sQuery(id+"F0.wireOp",EDGE,"E1.left")])],"isStart":true})}),-1.0]])]});
            var Q3;
            Q3=makeQuery(id+"F2.opExtrude","CAP_FACE",FACE,{"disambiguationData":[OSD([sQuery(id+"F0.wireOp",EDGE,"E12"),sQuery(id+"F0.wireOp",EDGE,"E13"),sQuery(id+"F0.wireOp",EDGE,"E14"),sQuery(id+"F0.wireOp",EDGE,"E15"),sQuery(id+"F0.wireOp",EDGE,"E17.filletArc"),sQuery(id+"F0.wireOp",EDGE,"E18.filletArc"),sQuery(id+"F0.wireOp",EDGE,"E19.filletArc"),sQuery(id+"F0.wireOp",EDGE,"E20.filletArc"),sQuery(id+"F0.wireOp",EDGE,"E25.0"),sQuery(id+"F0.wireOp",EDGE,"E25.1"),sQuery(id+"F0.wireOp",EDGE,"E25.2"),sQuery(id+"F0.wireOp",EDGE,"E25.3"),sQuery(id+"F0.wireOp",EDGE,"E25.4"),sQuery(id+"F0.wireOp",EDGE,"E25.5"),sQuery(id+"F0.wireOp",EDGE,"E25.6"),sQuery(id+"F0.wireOp",EDGE,"E25.7")])],"isStart":false});
            extrude(context, id + "F17", {"entities" : qUnion([Q0, Q1, Q2]), "endBound" : BoundingType.UP_TO_SURFACE, "endBoundEntityFace" : qUnion([Q3]), "depth" : 25 * mm, "offsetDistance" : 25 * mm});
        }
    });
